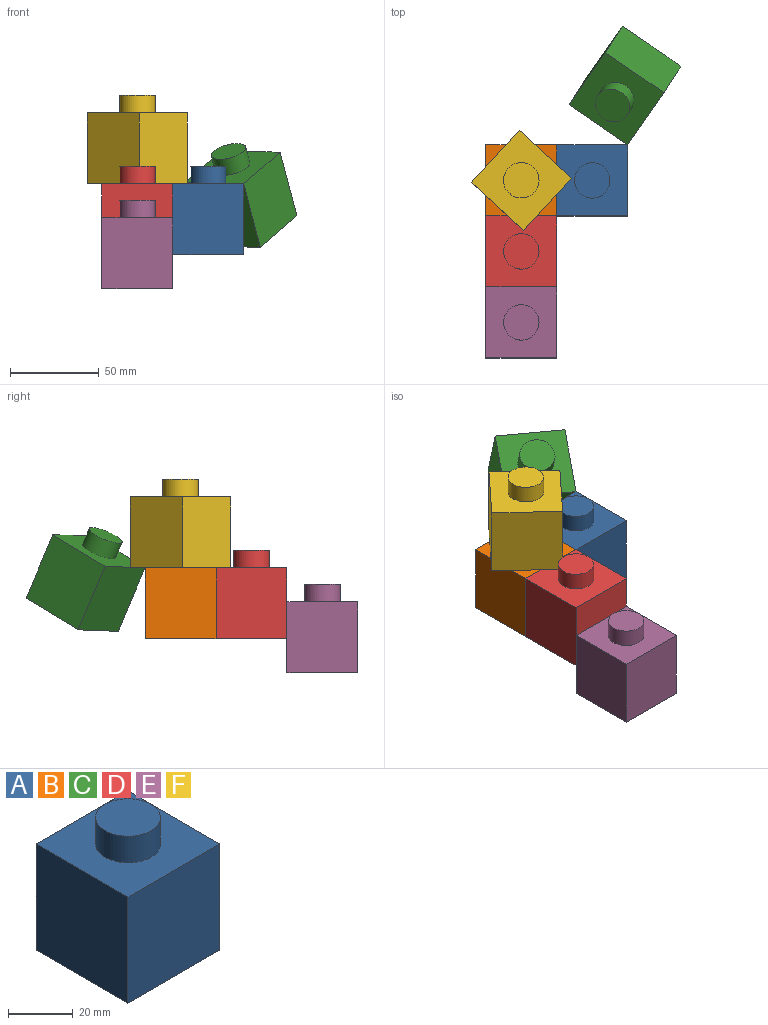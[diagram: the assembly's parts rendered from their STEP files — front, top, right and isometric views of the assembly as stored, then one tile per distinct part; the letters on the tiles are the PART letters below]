
ASSEMBLY  parts=6 mates=5
PART A: 10 faces, bbox 40x40x50 mm
  f0: plane 40x40mm, normal (0,-1,0), area 1600mm2, adj f1,f3,f4,f5
  f1: plane 40x40mm, normal (1,0,0), area 1600mm2, adj f0,f2,f4,f5
  f2: plane 40x40mm, normal (0,1,0), area 1600mm2, adj f1,f3,f4,f5
  f3: plane 40x40mm, normal (-1,0,0), area 1600mm2, adj f0,f2,f4,f5
  f4: plane 40x40mm, normal (0,0,1), area 1285.8mm2, adj f0,f1,f2,f3,f6
  f5: plane 40x40mm, normal (0,0,-1), area 1285.8mm2, adj f0,f1,f2,f3,f8
  f6: cylinder r=10mm len=20mm, axis (0,0,-1), area 628.3mm2, adj f4,f7
  f7: plane 20x20mm, normal (0,0,1), area 314.2mm2, adj f6
  f8: cylinder r=10mm len=20mm, axis (0,0,-1), area 628.3mm2, adj f5,f9
  f9: plane 20x20mm, normal (0,0,-1), area 314.2mm2, adj f8
PART B: same geometry as A
PART C: same geometry as A
PART D: same geometry as A
PART E: same geometry as A
PART F: same geometry as A
PLACE A t=(141.3,-57.11,-201.5)mm
PLACE B t=(101.3,-57.11,-201.5)mm fixed
PLACE C rot(axis=(0.23,-0.39,0.89),60.9deg) t=(164.48,3.99,-187.97)mm
PLACE D t=(101.3,-97.11,-201.5)mm
PLACE E t=(101.3,-137.11,-220.7)mm
PLACE F rot(axis=(0,0,1),47.3deg) t=(101.3,-57.11,-161.5)mm
MATE fastened B.f5 <-> D.f5  axis (0,0,1) through (81.3,-77.11,-201.5)mm
MATE revolute F.f8 <-> B.f6  axis (0,0,-1) through (101.3,-57.11,-151.5)mm
MATE fastened B.f4 <-> A.f4  axis (0,0,1) through (121.3,-37.11,-161.5)mm
MATE slider D.f4 <-> E.f4  axis (0,0,1) through (121.3,-117.11,-161.5)mm
MATE ball A.f4 <-> C.f4  axis (0,0,1) through (161.3,-37.11,-161.5)mm
